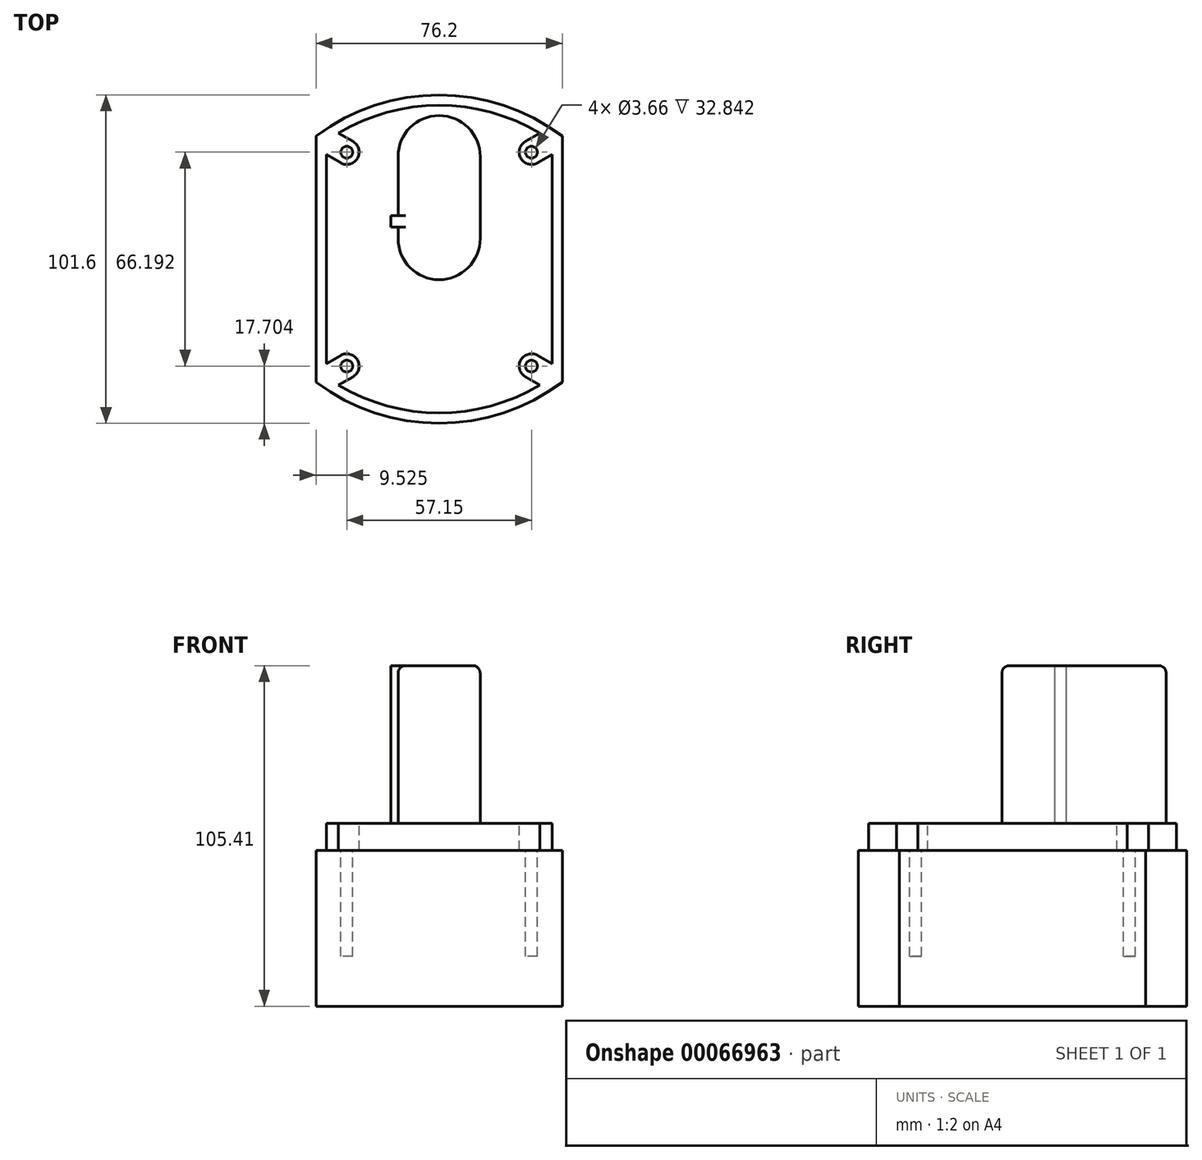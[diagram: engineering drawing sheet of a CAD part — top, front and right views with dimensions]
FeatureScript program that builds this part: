
annotation { "Feature Type Name" : "Feature", "Feature Type Description" : "" }
export const myFeature = defineFeature(function(context is Context, id is Id, definition is map)
    precondition{}
    {
        {
            var Q0;
            Q0=qCreatedBy(makeId("Top.planeOp"),FACE);
            var sketch = newSketch(context, id + "F0", { "sketchPlane" : qUnion([Q0])});
            skLineSegment(sketch, "E0.rect.bottom", {"start": v(38.1, -38.1) * mm, "end": v(-38.1, -38.1) * mm, "construction": true});
            skLineSegment(sketch, "E0.rect.top", {"start": v(38.1, 38.1) * mm, "end": v(-38.1, 38.1) * mm, "construction": true});
            skLineSegment(sketch, "E0.rect.left", {"start": v(38.1, -38.1) * mm, "end": v(38.1, 38.1) * mm});
            skLineSegment(sketch, "E0.rect.right", {"start": v(-38.1, -38.1) * mm, "end": v(-38.1, 38.1) * mm});
            skPoint(sketch, "E0.rect.middle", {"position": v(0, 0) * mm});
            skPoint(sketch, "E1.endSnap0", {"position": v(0, 38.1) * mm});
            skLineSegment(sketch, "E2", {"start": v(0, 38.1) * mm, "end": v(0, 50.8) * mm, "construction": true});
            skArc(sketch, "E3", {"start": v(38.1, 38.1) * mm, "mid": v(0, 50.8) * mm, "end": v(-38.1, 38.1) * mm});
            skLineSegment(sketch, "E4", {"start": v(-38.1, 0) * mm, "end": v(38.1, 0) * mm, "construction": true});
            skArc(sketch, "E5.MirrorCS", {"start": v(38.1, -38.1) * mm, "mid": v(0, -50.8) * mm, "end": v(-38.1, -38.1) * mm});
            skSolve(sketch);
        }
        {
            var Q0;
            Q0 = qSketchRegion(id + "F0", true);
            extrude(context, id + "F1", {"entities" : qUnion([Q0]), "oppositeDirection" : true, "depth" : 48.26 * mm});
        }
        {
            var Q0;
            Q0=makeQuery(id+"F1.opExtrude","CAP_FACE",FACE,{"disambiguationData":[OSD([sQuery(id+"F0.wireOp",EDGE,"E0.rect.left"),sQuery(id+"F0.wireOp",EDGE,"E0.rect.right"),sQuery(id+"F0.wireOp",EDGE,"E3"),sQuery(id+"F0.wireOp",EDGE,"E5.MirrorCS")])],"isStart":true});
            var sketch = newSketch(context, id + "F2", { "sketchPlane" : qUnion([Q0])});
            skArc(sketch, "E6.0.0", {"start": v(-38.1, -38.1) * mm, "mid": v(0, -50.8) * mm, "end": v(38.1, -38.1) * mm, "construction": true});
            skLineSegment(sketch, "E6.0.1", {"start": v(38.1, -38.1) * mm, "end": v(38.1, 38.1) * mm, "construction": true});
            skArc(sketch, "E6.0.2", {"start": v(38.1, 38.1) * mm, "mid": v(0, 50.8) * mm, "end": v(-38.1, 38.1) * mm, "construction": true});
            skLineSegment(sketch, "E6.0.3", {"start": v(-38.1, 38.1) * mm, "end": v(-38.1, -38.1) * mm, "construction": true});
            skArc(sketch, "E7.0", {"start": v(-34.92, -36.49) * mm, "mid": v(0, -47.62) * mm, "end": v(34.92, -36.49) * mm});
            skLineSegment(sketch, "E7.1", {"start": v(-34.93, 36.49) * mm, "end": v(-34.93, -36.49) * mm});
            skArc(sketch, "E7.2", {"start": v(34.93, 36.49) * mm, "mid": v(0, 47.63) * mm, "end": v(-34.92, 36.49) * mm});
            skLineSegment(sketch, "E7.3", {"start": v(34.93, -36.49) * mm, "end": v(34.93, 36.49) * mm});
            skSolve(sketch);
        }
        {
            var Q0;
            Q0 = qSketchRegion(id + "F2", true);
            extrude(context, id + "F3", {"entities" : qUnion([Q0]), "operationType" : NewBodyOperationType.ADD, "depth" : 8.38 * mm});
        }
        {
            var Q0;
            Q0=makeQuery(id+"F3.opExtrude","CAP_FACE",FACE,{"disambiguationData":[OSD([sQuery(id+"F2.wireOp",EDGE,"E7.0"),sQuery(id+"F2.wireOp",EDGE,"E7.1"),sQuery(id+"F2.wireOp",EDGE,"E7.2"),sQuery(id+"F2.wireOp",EDGE,"E7.3")])],"isStart":false});
            var sketch = newSketch(context, id + "F4", { "sketchPlane" : qUnion([Q0])});
            skLineSegment(sketch, "E8.rect.bottom", {"start": v(28.57, -33.1) * mm, "end": v(-28.58, -33.1) * mm, "construction": true});
            skLineSegment(sketch, "E8.rect.top", {"start": v(28.58, 33.1) * mm, "end": v(-28.57, 33.1) * mm, "construction": true});
            skLineSegment(sketch, "E8.rect.left", {"start": v(28.57, -33.1) * mm, "end": v(28.58, 33.1) * mm, "construction": true});
            skLineSegment(sketch, "E8.rect.right", {"start": v(-28.58, -33.1) * mm, "end": v(-28.57, 33.1) * mm, "construction": true});
            skPoint(sketch, "E8.rect.middle", {"position": v(0, 0) * mm});
            skLineSegment(sketch, "E9", {"start": v(-28.57, -33.1) * mm, "end": v(-50.57, -45.8) * mm, "construction": true});
            skArc(sketch, "E10.0.startCap", {"start": v(-30.48, -29.8) * mm, "mid": v(-25.28, -31.2) * mm, "end": v(-26.67, -36.4) * mm});
            skArc(sketch, "E10.0.endCap", {"start": v(-48.67, -49.1) * mm, "mid": v(-53.87, -47.7) * mm, "end": v(-52.48, -42.5) * mm});
            skLineSegment(sketch, "E10.0.left", {"start": v(-26.67, -36.4) * mm, "end": v(-48.67, -49.1) * mm});
            skLineSegment(sketch, "E10.0.right", {"start": v(-30.48, -29.8) * mm, "end": v(-52.48, -42.5) * mm});
            skLineSegment(sketch, "E11", {"start": v(-28.58, 0) * mm, "end": v(28.58, 0) * mm, "construction": true});
            skLineSegment(sketch, "E12", {"start": v(0, 33.1) * mm, "end": v(0, -33.1) * mm, "construction": true});
            skLineSegment(sketch, "E13.MirrorCS", {"start": v(30.48, -29.8) * mm, "end": v(52.48, -42.5) * mm});
            skArc(sketch, "E14.MirrorCS", {"start": v(48.67, -49.1) * mm, "mid": v(53.87, -47.7) * mm, "end": v(52.48, -42.5) * mm});
            skLineSegment(sketch, "E15.MirrorCS", {"start": v(26.67, -36.4) * mm, "end": v(48.67, -49.1) * mm});
            skArc(sketch, "E16.MirrorCS", {"start": v(30.48, -29.8) * mm, "mid": v(25.28, -31.2) * mm, "end": v(26.67, -36.4) * mm});
            skLineSegment(sketch, "E17.MirrorCS", {"start": v(-30.48, 29.8) * mm, "end": v(-52.48, 42.5) * mm});
            skArc(sketch, "E18.MirrorCS", {"start": v(-48.67, 49.1) * mm, "mid": v(-53.87, 47.7) * mm, "end": v(-52.48, 42.5) * mm});
            skLineSegment(sketch, "E19.MirrorCS", {"start": v(-26.67, 36.4) * mm, "end": v(-48.67, 49.1) * mm});
            skArc(sketch, "E20.MirrorCS", {"start": v(-30.48, 29.8) * mm, "mid": v(-25.28, 31.2) * mm, "end": v(-26.67, 36.4) * mm});
            skArc(sketch, "E21.MirrorCS", {"start": v(30.48, 29.8) * mm, "mid": v(25.28, 31.2) * mm, "end": v(26.67, 36.4) * mm});
            skLineSegment(sketch, "E22.MirrorCS", {"start": v(26.67, 36.4) * mm, "end": v(48.67, 49.1) * mm});
            skLineSegment(sketch, "E23.MirrorCS", {"start": v(30.48, 29.8) * mm, "end": v(52.48, 42.5) * mm});
            skArc(sketch, "E24.MirrorCS", {"start": v(48.67, 49.1) * mm, "mid": v(53.87, 47.7) * mm, "end": v(52.48, 42.5) * mm});
            skCircle(sketch, "E25", {"center": v(-28.57, 33.1) * mm, "radius": 1.83 * mm, "construction": true});
            skCircle(sketch, "E26", {"center": v(28.58, 33.1) * mm, "radius": 1.83 * mm, "construction": true});
            skCircle(sketch, "E27", {"center": v(-28.58, -33.1) * mm, "radius": 1.83 * mm, "construction": true});
            skCircle(sketch, "E28", {"center": v(28.57, -33.1) * mm, "radius": 1.83 * mm, "construction": true});
            skSolve(sketch);
        }
        {
            var Q0;
            Q0 = qSketchRegion(id + "F4", true);
            var Q1;
            Q1=makeQuery(id+"F1.opExtrude","CAP_FACE",FACE,{"disambiguationData":[OSD([sQuery(id+"F0.wireOp",EDGE,"E0.rect.left"),sQuery(id+"F0.wireOp",EDGE,"E0.rect.right"),sQuery(id+"F0.wireOp",EDGE,"E3"),sQuery(id+"F0.wireOp",EDGE,"E5.MirrorCS")])],"isStart":true});
            extrude(context, id + "F5", {"entities" : qUnion([Q0]), "operationType" : NewBodyOperationType.REMOVE, "endBound" : BoundingType.UP_TO_SURFACE, "oppositeDirection" : true, "endBoundEntityFace" : qUnion([Q1]), "depth" : 25.4 * mm});
        }
        {
            var Q0;
            Q0=makeQuery(id+"F5.boolean.opBoolean","MERGE",FACE,{"derivedFrom":[makeQuery(id+"F1.opExtrude","CAP_FACE",FACE,{"disambiguationData":[OSD([sQuery(id+"F0.wireOp",EDGE,"E0.rect.left"),sQuery(id+"F0.wireOp",EDGE,"E0.rect.right"),sQuery(id+"F0.wireOp",EDGE,"E3"),sQuery(id+"F0.wireOp",EDGE,"E5.MirrorCS")])],"isStart":true}),makeQuery(id+"F5.opExtrude","CAP_FACE",FACE,{"disambiguationData":[OSD([sQuery(id+"F4.wireOp",EDGE,"E10.0.startCap"),sQuery(id+"F4.wireOp",EDGE,"E10.0.endCap"),sQuery(id+"F4.wireOp",EDGE,"E10.0.left"),sQuery(id+"F4.wireOp",EDGE,"E10.0.right")])],"isStart":false}),makeQuery(id+"F5.opExtrude","CAP_FACE",FACE,{"disambiguationData":[OSD([sQuery(id+"F4.wireOp",EDGE,"E13.MirrorCS"),sQuery(id+"F4.wireOp",EDGE,"E14.MirrorCS"),sQuery(id+"F4.wireOp",EDGE,"E15.MirrorCS"),sQuery(id+"F4.wireOp",EDGE,"E16.MirrorCS")])],"isStart":false}),makeQuery(id+"F5.opExtrude","CAP_FACE",FACE,{"disambiguationData":[OSD([sQuery(id+"F4.wireOp",EDGE,"E17.MirrorCS"),sQuery(id+"F4.wireOp",EDGE,"E18.MirrorCS"),sQuery(id+"F4.wireOp",EDGE,"E19.MirrorCS"),sQuery(id+"F4.wireOp",EDGE,"E20.MirrorCS")])],"isStart":false}),makeQuery(id+"F5.opExtrude","CAP_FACE",FACE,{"disambiguationData":[OSD([sQuery(id+"F4.wireOp",EDGE,"E21.MirrorCS"),sQuery(id+"F4.wireOp",EDGE,"E22.MirrorCS"),sQuery(id+"F4.wireOp",EDGE,"E23.MirrorCS"),sQuery(id+"F4.wireOp",EDGE,"E24.MirrorCS")])],"isStart":false})]});
            var sketch = newSketch(context, id + "F6", { "sketchPlane" : qUnion([Q0])});
            skCircle(sketch, "E29.0", {"center": v(-28.57, 33.1) * mm, "radius": 1.83 * mm});
            skCircle(sketch, "E29.1", {"center": v(28.58, 33.1) * mm, "radius": 1.83 * mm});
            skCircle(sketch, "E29.2", {"center": v(28.57, -33.1) * mm, "radius": 1.83 * mm});
            skCircle(sketch, "E29.3", {"center": v(-28.58, -33.1) * mm, "radius": 1.83 * mm});
            skSolve(sketch);
        }
        {
            var Q0;
            Q0 = qSketchRegion(id + "F6", true);
            extrude(context, id + "F7", {"entities" : qUnion([Q0]), "operationType" : NewBodyOperationType.REMOVE, "oppositeDirection" : true, "depth" : 32.84 * mm});
        }
        {
            var Q0;
            Q0=makeQuery(id+"F6.imprint","IMPRINT",FACE,{"disambiguationData":[TD([[makeQuery(id+"F6.imprint","IMPRINT",EDGE,{"derivedFrom":sQuery(id+"F6.wireOp",EDGE,"E29.0")}),-1.0]])]});
            var sketch = newSketch(context, id + "F8", { "sketchPlane" : qUnion([Q0])});
            skCircle(sketch, "E30.0", {"center": v(-28.57, 33.1) * mm, "radius": 1.83 * mm});
            skCircle(sketch, "E30.1", {"center": v(28.58, 33.1) * mm, "radius": 1.83 * mm});
            skCircle(sketch, "E30.2", {"center": v(28.57, -33.1) * mm, "radius": 1.83 * mm});
            skCircle(sketch, "E30.3", {"center": v(-28.58, -33.1) * mm, "radius": 1.83 * mm});
            skSolve(sketch);
        }
        {
            var Q0;
            Q0 = qSketchRegion(id + "F8", true);
            extrude(context, id + "F9", {"entities" : qUnion([Q0]), "operationType" : NewBodyOperationType.REMOVE, "oppositeDirection" : true, "depth" : 32.84 * mm});
        }
        {
            var Q0;
            Q0=qCreatedBy(makeId("Top.planeOp"),FACE);
            var sketch = newSketch(context, id + "F10", { "sketchPlane" : qUnion([Q0])});
            skLineSegment(sketch, "E31", {"start": v(0, 6.35) * mm, "end": v(0, 31.75) * mm, "construction": true});
            skArc(sketch, "E32.0.startCap", {"start": v(12.7, 6.35) * mm, "mid": v(0, -6.35) * mm, "end": v(-12.7, 6.35) * mm});
            skArc(sketch, "E32.0.endCap", {"start": v(-12.7, 31.75) * mm, "mid": v(0, 44.45) * mm, "end": v(12.7, 31.75) * mm});
            skLineSegment(sketch, "E32.0.left", {"start": v(-12.7, 6.35) * mm, "end": v(-12.7, 31.75) * mm});
            skLineSegment(sketch, "E32.0.right", {"start": v(12.7, 6.35) * mm, "end": v(12.7, 31.75) * mm});
            skPoint(sketch, "E33", {"position": v(0, 19.05) * mm});
            skPoint(sketch, "E34", {"position": v(0, 44.45) * mm});
            skPoint(sketch, "E35", {"position": v(0, -6.35) * mm});
            skSolve(sketch);
        }
        {
            var Q0;
            Q0 = qSketchRegion(id + "F10", true);
            extrude(context, id + "F11", {"entities" : qUnion([Q0]), "operationType" : NewBodyOperationType.ADD, "depth" : 57.15 * mm});
        }
        {
            var Q0;
            Q0=makeQuery(id+"F3.opExtrude","CAP_FACE",FACE,{"disambiguationData":[OSD([sQuery(id+"F2.wireOp",EDGE,"E7.0"),sQuery(id+"F2.wireOp",EDGE,"E7.1"),sQuery(id+"F2.wireOp",EDGE,"E7.2"),sQuery(id+"F2.wireOp",EDGE,"E7.3")])],"isStart":false});
            var sketch = newSketch(context, id + "F12", { "sketchPlane" : qUnion([Q0])});
            skLineSegment(sketch, "E36.bottom", {"start": v(-12.7, 13.46) * mm, "end": v(-14.99, 13.46) * mm});
            skLineSegment(sketch, "E36.top", {"start": v(-12.7, 9.9) * mm, "end": v(-14.99, 9.9) * mm});
            skLineSegment(sketch, "E36.left", {"start": v(-12.7, 13.46) * mm, "end": v(-12.7, 9.9) * mm});
            skLineSegment(sketch, "E36.right", {"start": v(-14.99, 13.46) * mm, "end": v(-14.99, 9.9) * mm});
            skSolve(sketch);
        }
        {
            var Q0;
            Q0 = qSketchRegion(id + "F12", true);
            var Q1;
            Q1=makeQuery(id+"F11.opExtrude","CAP_FACE",FACE,{"disambiguationData":[OSD([sQuery(id+"F10.wireOp",EDGE,"E32.0.startCap"),sQuery(id+"F10.wireOp",EDGE,"E32.0.endCap"),sQuery(id+"F10.wireOp",EDGE,"E32.0.left"),sQuery(id+"F10.wireOp",EDGE,"E32.0.right")])],"isStart":false});
            extrude(context, id + "F13", {"entities" : qUnion([Q0]), "operationType" : NewBodyOperationType.ADD, "endBound" : BoundingType.UP_TO_SURFACE, "endBoundEntityFace" : qUnion([Q1]), "depth" : 25.4 * mm});
        }
        {
            var Q0;
            Q0=makeQuery(id+"F11.opExtrude","CAP_EDGE",EDGE,{"disambiguationData":[OSD([sQuery(id+"F10.wireOp",EDGE,"E32.0.right")])],"isStart":false});
            fillet(context, id + "F14", {"entities" : qUnion([Q0]), "radius" : 2.3 * mm, "tangentPropagation" : true, "allowEdgeOverflow" : false});
        }
    });
